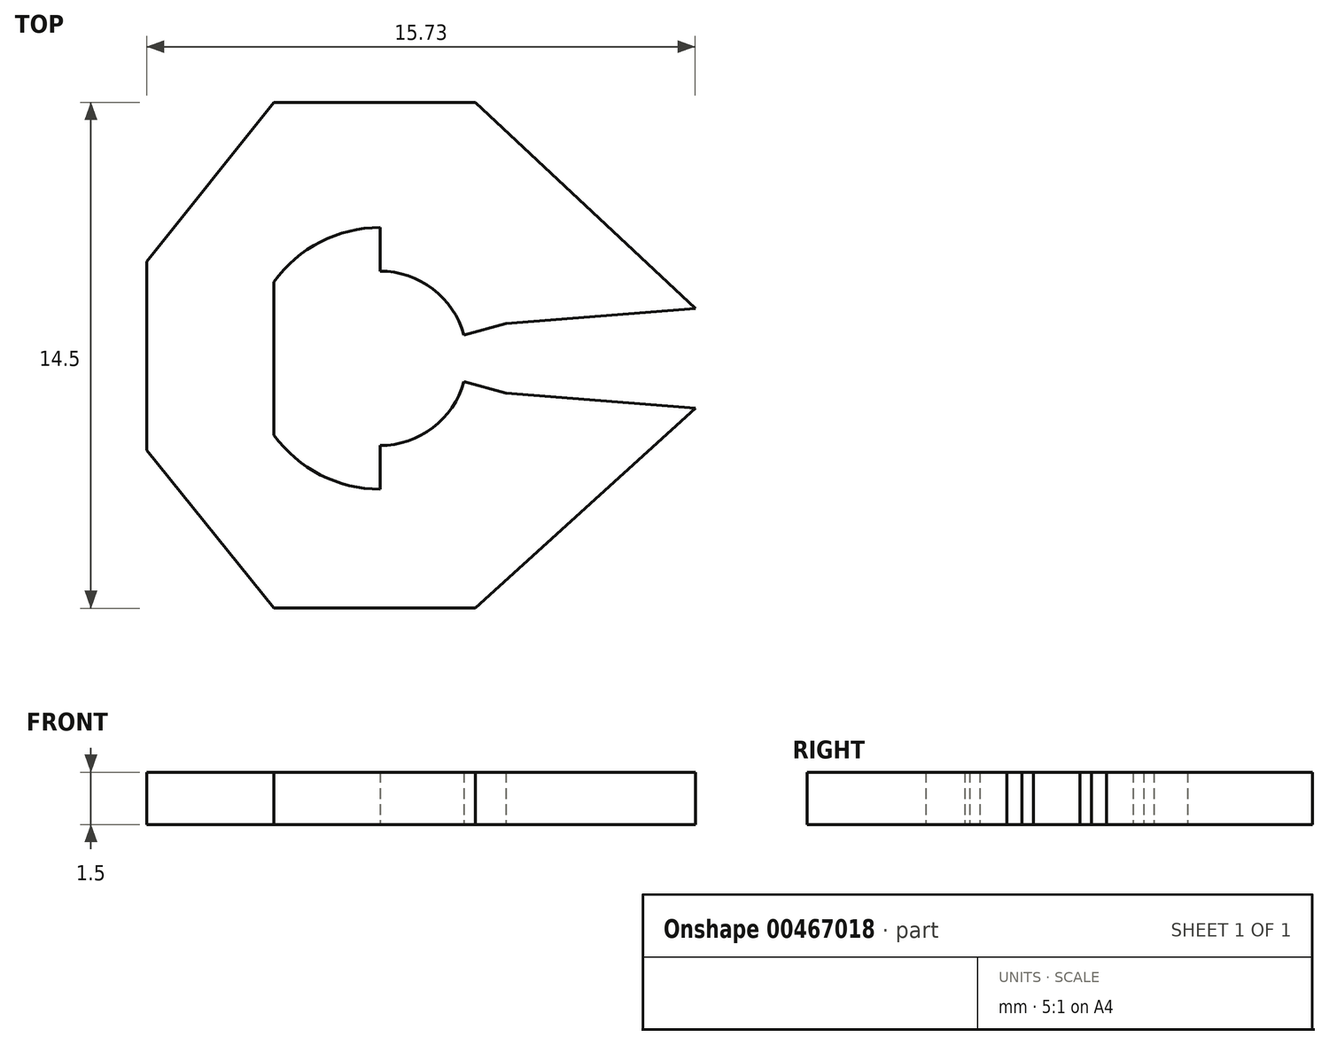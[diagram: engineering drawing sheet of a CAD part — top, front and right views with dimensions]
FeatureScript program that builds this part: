
annotation { "Feature Type Name" : "Feature", "Feature Type Description" : "" }
export const myFeature = defineFeature(function(context is Context, id is Id, definition is map)
    precondition{}
    {
        {
            var Q0;
            Q0=qCreatedBy(makeId("Top.planeOp"),FACE);
            var sketch = newSketch(context, id + "F0", { "sketchPlane" : qUnion([Q0])});
            skPoint(sketch, "E0.middle", {"position": v(0, 0) * mm});
            skPoint(sketch, "E1", {"position": v(-7.5, 1.66) * mm});
            skCircle(sketch, "E2", {"center": v(-7.5, 1.66) * mm, "radius": 3.75 * mm});
            skLineSegment(sketch, "E3", {"start": v(-7.5, 1.66) * mm, "end": v(-7.5, 5.41) * mm});
            skLineSegment(sketch, "E4", {"start": v(-7.5, 1.66) * mm, "end": v(-7.5, -2.09) * mm});
            skLineSegment(sketch, "E5", {"start": v(-7.5, 1.66) * mm, "end": v(-11.25, 1.66) * mm});
            skLineSegment(sketch, "E6", {"start": v(-7.5, 1.66) * mm, "end": v(-3.89, 2.66) * mm});
            skLineSegment(sketch, "E7", {"start": v(-7.5, 1.66) * mm, "end": v(-3.89, 0.66) * mm});
            skCircle(sketch, "E8", {"center": v(-7.5, 1.66) * mm, "radius": 2.5 * mm});
            skLineSegment(sketch, "E9", {"start": v(1.54, 9) * mm, "end": v(1.54, -5.5) * mm});
            skLineSegment(sketch, "E10", {"start": v(1.54, 3.1) * mm, "end": v(-3.89, 2.66) * mm});
            skLineSegment(sketch, "E11", {"start": v(-3.89, 0.66) * mm, "end": v(1.54, 0.23) * mm});
            skLineSegment(sketch, "E12", {"start": v(-14.2, 9) * mm, "end": v(-14.2, -5.5) * mm});
            skLineSegment(sketch, "E13", {"start": v(-14.2, 9) * mm, "end": v(1.54, 9) * mm});
            skLineSegment(sketch, "E14", {"start": v(-14.2, -5.5) * mm, "end": v(1.54, -5.5) * mm});
            skLineSegment(sketch, "E15", {"start": v(-7.5, 1.66) * mm, "end": v(-9.92, 4.53) * mm});
            skLineSegment(sketch, "E16", {"start": v(-7.5, 1.66) * mm, "end": v(-10.03, -1.1) * mm});
            skLineSegment(sketch, "E17", {"start": v(1.54, 0.23) * mm, "end": v(-4.76, -5.5) * mm});
            skLineSegment(sketch, "E18", {"start": v(-4.76, -5.5) * mm, "end": v(-4.76, 9) * mm});
            skLineSegment(sketch, "E19", {"start": v(1.54, 3.1) * mm, "end": v(-4.76, 9) * mm});
            skLineSegment(sketch, "E20", {"start": v(-10.54, 9) * mm, "end": v(-10.54, -5.5) * mm});
            skLineSegment(sketch, "E21", {"start": v(-10.54, 9) * mm, "end": v(-14.2, 4.45) * mm});
            skLineSegment(sketch, "E22", {"start": v(-10.54, -5.5) * mm, "end": v(-14.2, -0.97) * mm});
            skSolve(sketch);
        }
        {
            var Q0;
            {var subQ8=sQuery(id+"F0.wireOp",EDGE,"SGAB5Jx7-oL00-DTdC-0CY0-yKzGlIMBEJJ3");Q0=makeQuery(id+"F0.imprint","IMPRINT",FACE,{"disambiguationData":[TD([[makeQuery(id+"F0.imprint","IMPRINT",EDGE,{"derivedFrom":subQ8}),-1.0]])]});}
            var Q1;
            {var subQ7=sQuery(id+"F0.wireOp",EDGE,"mMa6P0aA-eIxY-Aoy9-Eim0-QecPNGlAzSQc");Q1=makeQuery(id+"F0.imprint","IMPRINT",FACE,{"disambiguationData":[TD([[makeQuery(id+"F0.imprint","IMPRINT",EDGE,{"derivedFrom":subQ7}),-1.0]])]});}
            var Q2;
            {var subQ5=sQuery(id+"F0.wireOp",EDGE,"E0.top");Q2=makeQuery(id+"F0.imprint","IMPRINT",FACE,{"disambiguationData":[TD([[makeQuery(id+"F0.imprint","IMPRINT",EDGE,{"derivedFrom":subQ5}),1.0]])]});}
            var Q3;
            {var subQ5=sQuery(id+"F0.wireOp",EDGE,"E10");Q3=makeQuery(id+"F0.imprint","IMPRINT",FACE,{"disambiguationData":[TD([[makeQuery(id+"F0.imprint","IMPRINT",EDGE,{"derivedFrom":subQ5}),-1.0]])]});}
            var Q4;
            {var subQ0=sQuery(id+"F0.wireOp",EDGE,"E4");var subQ1=sQuery(id+"F0.wireOp",EDGE,"E2");var subQ2=makeQuery(id+"F0.imprint","INTERSECT",VERTEX,{"derivedFrom":[subQ1,subQ0]});Q4=makeQuery(id+"F0.imprint","IMPRINT",FACE,{"disambiguationData":[TD([[makeQuery(id+"F0.imprint","IMPRINT",EDGE,{"disambiguationData":[TD([[subQ2,1.0]])],"derivedFrom":subQ0}),1.0]])]});}
            var Q5;
            {var subQ0=sQuery(id+"F0.wireOp",EDGE,"E3");var subQ1=sQuery(id+"F0.wireOp",EDGE,"E2");var subQ2=makeQuery(id+"F0.imprint","INTERSECT",VERTEX,{"derivedFrom":[subQ1,subQ0]});Q5=makeQuery(id+"F0.imprint","IMPRINT",FACE,{"disambiguationData":[TD([[makeQuery(id+"F0.imprint","IMPRINT",EDGE,{"disambiguationData":[TD([[subQ2,1.0]])],"derivedFrom":subQ0}),-1.0]])]});}
            var Q6;
            {var subQ0=sQuery(id+"F0.wireOp",EDGE,"E5");var subQ1=sQuery(id+"F0.wireOp",EDGE,"E2");var subQ2=makeQuery(id+"F0.imprint","INTERSECT",VERTEX,{"derivedFrom":[subQ1,subQ0]});Q6=makeQuery(id+"F0.imprint","IMPRINT",FACE,{"disambiguationData":[TD([[makeQuery(id+"F0.imprint","IMPRINT",EDGE,{"disambiguationData":[TD([[subQ2,1.0]])],"derivedFrom":subQ1}),1.0]])]});}
            var Q7;
            {var subQ0=sQuery(id+"F0.wireOp",EDGE,"E5");var subQ1=sQuery(id+"F0.wireOp",EDGE,"E2");var subQ2=makeQuery(id+"F0.imprint","INTERSECT",VERTEX,{"derivedFrom":[subQ1,subQ0]});Q7=makeQuery(id+"F0.imprint","IMPRINT",FACE,{"disambiguationData":[TD([[makeQuery(id+"F0.imprint","IMPRINT",EDGE,{"disambiguationData":[TD([[subQ2,-1.0]])],"derivedFrom":subQ1}),1.0]])]});}
            var Q8;
            {var subQ0=sQuery(id+"F0.wireOp",EDGE,"E11");Q8=makeQuery(id+"F0.imprint","IMPRINT",FACE,{"disambiguationData":[TD([[makeQuery(id+"F0.imprint","IMPRINT",EDGE,{"derivedFrom":subQ0}),-1.0]])]});}
            var Q9;
            {var subQ5=sQuery(id+"F0.wireOp",EDGE,"E2");var subQ8=makeQuery(id+"F0.imprint","INTERSECT",VERTEX,{"derivedFrom":[subQ5,sQuery(id+"F0.wireOp",EDGE,"E16")]});Q9=makeQuery(id+"F0.imprint","IMPRINT",FACE,{"disambiguationData":[TD([[makeQuery(id+"F0.imprint","IMPRINT",EDGE,{"disambiguationData":[TD([[subQ8,1.0]])],"derivedFrom":subQ5}),-1.0]])]});}
            var Q10;
            {var subQ5=sQuery(id+"F0.wireOp",EDGE,"E2");var subQ8=makeQuery(id+"F0.imprint","INTERSECT",VERTEX,{"derivedFrom":[subQ5,sQuery(id+"F0.wireOp",EDGE,"E3")]});Q10=makeQuery(id+"F0.imprint","IMPRINT",FACE,{"disambiguationData":[TD([[makeQuery(id+"F0.imprint","IMPRINT",EDGE,{"disambiguationData":[TD([[subQ8,1.0]])],"derivedFrom":subQ5}),-1.0]])]});}
            var Q11;
            {var subQ0=sQuery(id+"F0.wireOp",EDGE,"E21");Q11=makeQuery(id+"F0.imprint","IMPRINT",FACE,{"disambiguationData":[TD([[makeQuery(id+"F0.imprint","IMPRINT",EDGE,{"derivedFrom":subQ0}),1.0]])]});}
            var Q12;
            {var subQ1=sQuery(id+"F0.wireOp",EDGE,"E2");var subQ3=sQuery(id+"F0.wireOp",EDGE,"E18");var subQ4=makeQuery(id+"F0.imprint","INTERSECT",VERTEX,{"disambiguationData":[OD(1.0)],"derivedFrom":[subQ1,subQ3]});Q12=makeQuery(id+"F0.imprint","IMPRINT",FACE,{"disambiguationData":[TD([[makeQuery(id+"F0.imprint","IMPRINT",EDGE,{"disambiguationData":[TD([[subQ4,-1.0]])],"derivedFrom":subQ3}),-1.0]])]});}
            var Q13;
            {var subQ1=sQuery(id+"F0.wireOp",EDGE,"E2");var subQ3=sQuery(id+"F0.wireOp",EDGE,"E18");var subQ4=makeQuery(id+"F0.imprint","INTERSECT",VERTEX,{"disambiguationData":[OD(0.0)],"derivedFrom":[subQ1,subQ3]});Q13=makeQuery(id+"F0.imprint","IMPRINT",FACE,{"disambiguationData":[TD([[makeQuery(id+"F0.imprint","IMPRINT",EDGE,{"disambiguationData":[TD([[subQ4,1.0]])],"derivedFrom":subQ3}),-1.0]])]});}
            extrude(context, id + "F1", {"entities" : qUnion([Q0, Q1, Q2, Q3, Q4, Q5, Q6, Q7, Q8, Q9, Q10, Q11, Q12, Q13]), "depth" : 1.5 * mm});
        }
    });
